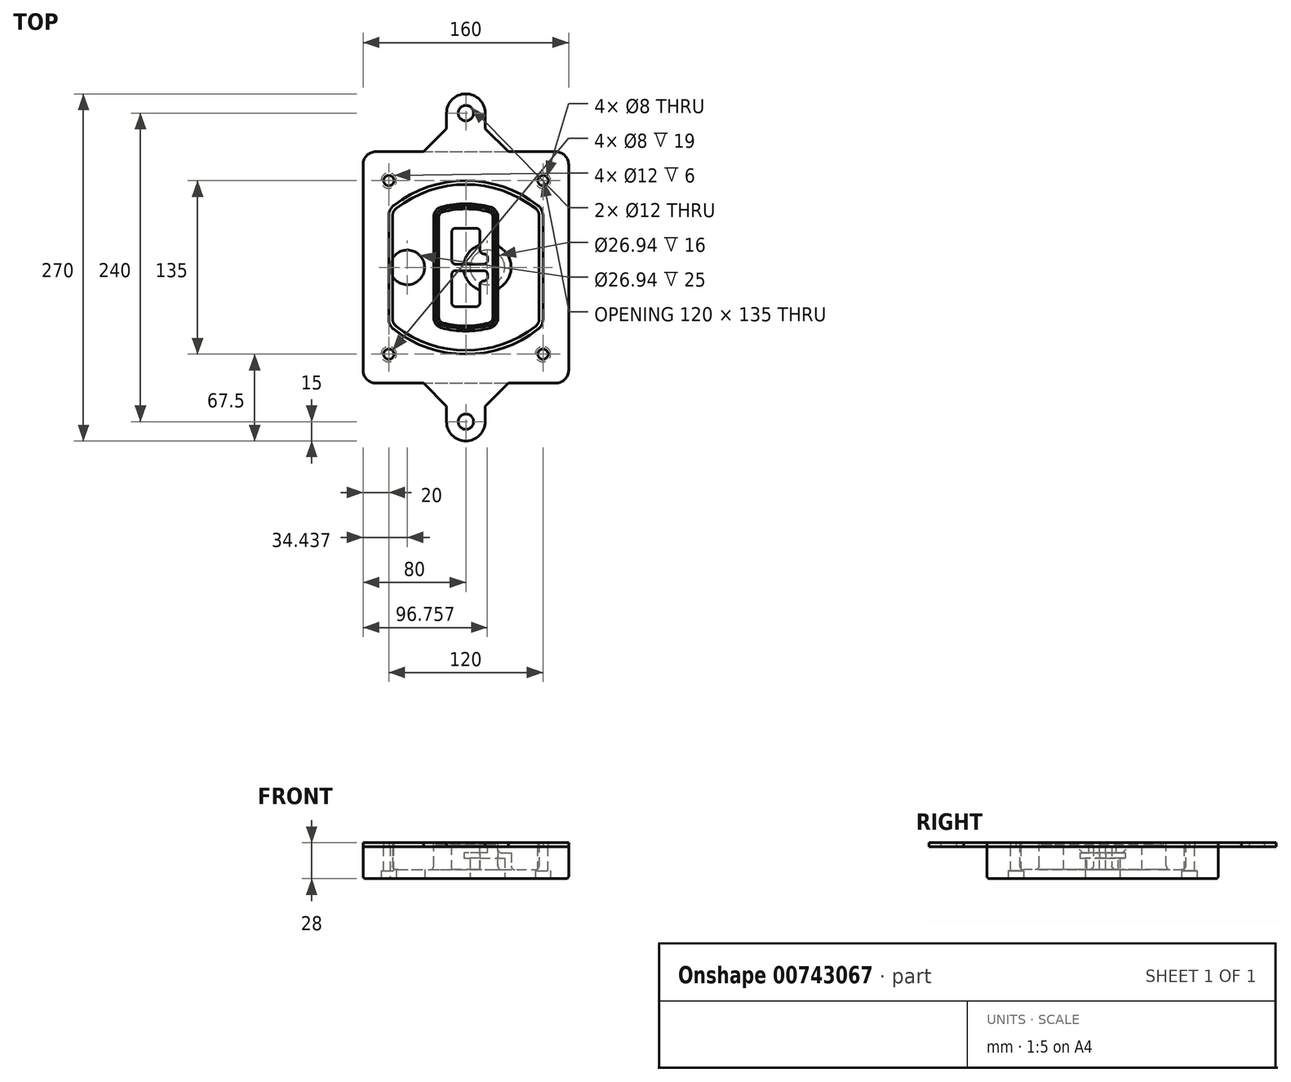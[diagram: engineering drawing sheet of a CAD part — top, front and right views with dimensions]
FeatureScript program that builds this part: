
annotation { "Feature Type Name" : "Feature", "Feature Type Description" : "" }
export const myFeature = defineFeature(function(context is Context, id is Id, definition is map)
    precondition{}
    {
        {
            var Q0;
            Q0=qCreatedBy(makeId("Top.planeOp"),FACE);
            var sketch = newSketch(context, id + "F0", { "sketchPlane" : qUnion([Q0])});
            skPoint(sketch, "E0.rect.middle", {"position": v(0, 0) * mm});
            skLineSegment(sketch, "E1.bottom", {"start": v(-70, -90) * mm, "end": v(70, -90) * mm});
            skLineSegment(sketch, "E1.top", {"start": v(-70, 90) * mm, "end": v(70, 90) * mm});
            skLineSegment(sketch, "E1.left", {"start": v(-80, -80) * mm, "end": v(-80, 80) * mm});
            skLineSegment(sketch, "E1.right", {"start": v(80, -80) * mm, "end": v(80, 80) * mm});
            skLineSegment(sketch, "E2", {"start": v(-80, 90) * mm, "end": v(80, -90) * mm, "construction": true});
            skLineSegment(sketch, "E3", {"start": v(80, 90) * mm, "end": v(-80, -90) * mm, "construction": true});
            skCircle(sketch, "E4", {"center": v(-60, 67.5) * mm, "radius": 4 * mm});
            skCircle(sketch, "E5", {"center": v(60, 67.5) * mm, "radius": 4 * mm});
            skCircle(sketch, "E6", {"center": v(60, -67.5) * mm, "radius": 4 * mm});
            skCircle(sketch, "E7", {"center": v(-60, -67.5) * mm, "radius": 4 * mm});
            skLineSegment(sketch, "E8", {"start": v(-60, 67.5) * mm, "end": v(60, 67.5) * mm, "construction": true});
            skLineSegment(sketch, "E9", {"start": v(60, 67.5) * mm, "end": v(60, -67.5) * mm, "construction": true});
            skLineSegment(sketch, "E10", {"start": v(60, -67.5) * mm, "end": v(-60, -67.5) * mm, "construction": true});
            skLineSegment(sketch, "E11", {"start": v(-60, -67.5) * mm, "end": v(-60, 67.5) * mm, "construction": true});
            skLineSegment(sketch, "E12", {"start": v(-60, 40.3) * mm, "end": v(-60, -40.3) * mm});
            skLineSegment(sketch, "E13", {"start": v(60, 40.3) * mm, "end": v(60, -40.3) * mm});
            skArc(sketch, "E14", {"start": v(56.15, 48.18) * mm, "mid": v(0, 67.5) * mm, "end": v(-56.15, 48.18) * mm});
            skArc(sketch, "E15", {"start": v(-56.15, -48.18) * mm, "mid": v(0, -67.5) * mm, "end": v(56.15, -48.18) * mm});
            skLineSegment(sketch, "E16", {"start": v(-60, 0) * mm, "end": v(60, 0) * mm, "construction": true});
            skPoint(sketch, "E17.visualSharp", {"position": v(-60, -45) * mm});
            skArc(sketch, "E17.filletArc", {"start": v(-60, -40.3) * mm, "mid": v(-58.99, -44.68) * mm, "end": v(-56.15, -48.18) * mm});
            skPoint(sketch, "E18.visualSharp", {"position": v(-60, 45) * mm});
            skArc(sketch, "E18.filletArc", {"start": v(-56.15, 48.18) * mm, "mid": v(-58.99, 44.68) * mm, "end": v(-60, 40.3) * mm});
            skPoint(sketch, "E19.visualSharp", {"position": v(60, 45) * mm});
            skArc(sketch, "E19.filletArc", {"start": v(60, 40.3) * mm, "mid": v(58.99, 44.68) * mm, "end": v(56.15, 48.18) * mm});
            skPoint(sketch, "E20.visualSharp", {"position": v(60, -45) * mm});
            skArc(sketch, "E20.filletArc", {"start": v(56.15, -48.18) * mm, "mid": v(58.99, -44.68) * mm, "end": v(60, -40.3) * mm});
            skPoint(sketch, "E21.visualSharp", {"position": v(-80, 90) * mm});
            skArc(sketch, "E21.filletArc", {"start": v(-70, 90) * mm, "mid": v(-77.07, 87.07) * mm, "end": v(-80, 80) * mm});
            skPoint(sketch, "E22.visualSharp", {"position": v(80, 90) * mm});
            skArc(sketch, "E22.filletArc", {"start": v(80, 80) * mm, "mid": v(77.07, 87.07) * mm, "end": v(70, 90) * mm});
            skPoint(sketch, "E23.visualSharp", {"position": v(80, -90) * mm});
            skArc(sketch, "E23.filletArc", {"start": v(70, -90) * mm, "mid": v(77.07, -87.07) * mm, "end": v(80, -80) * mm});
            skPoint(sketch, "E24.visualSharp", {"position": v(-80, -90) * mm});
            skArc(sketch, "E24.filletArc", {"start": v(-80, -80) * mm, "mid": v(-77.07, -87.07) * mm, "end": v(-70, -90) * mm});
            skArc(sketch, "E25.0", {"start": v(57, 40.3) * mm, "mid": v(56.3, 43.36) * mm, "end": v(54.3, 45.81) * mm});
            skLineSegment(sketch, "E25.1", {"start": v(57, 40.3) * mm, "end": v(57, -40.3) * mm});
            skArc(sketch, "E25.2", {"start": v(54.3, -45.81) * mm, "mid": v(56.3, -43.36) * mm, "end": v(57, -40.3) * mm});
            skArc(sketch, "E25.3", {"start": v(-54.3, -45.81) * mm, "mid": v(0, -64.5) * mm, "end": v(54.3, -45.81) * mm});
            skArc(sketch, "E25.4", {"start": v(-57, -40.3) * mm, "mid": v(-56.3, -43.36) * mm, "end": v(-54.3, -45.81) * mm});
            skArc(sketch, "E25.5", {"start": v(54.3, 45.81) * mm, "mid": v(0, 64.5) * mm, "end": v(-54.3, 45.81) * mm});
            skLineSegment(sketch, "E25.6", {"start": v(-57, 40.3) * mm, "end": v(-57, -40.3) * mm});
            skArc(sketch, "E25.7", {"start": v(-54.3, 45.81) * mm, "mid": v(-56.3, 43.36) * mm, "end": v(-57, 40.3) * mm});
            skArc(sketch, "E26.0", {"start": v(-58.62, 51.33) * mm, "mid": v(-62.58, 46.43) * mm, "end": v(-64, 40.3) * mm});
            skArc(sketch, "E26.1", {"start": v(58.62, 51.33) * mm, "mid": v(0, 71.5) * mm, "end": v(-58.62, 51.33) * mm});
            skArc(sketch, "E26.2", {"start": v(64, 40.3) * mm, "mid": v(62.58, 46.43) * mm, "end": v(58.62, 51.33) * mm});
            skLineSegment(sketch, "E26.3", {"start": v(64, 40.3) * mm, "end": v(64, -40.3) * mm});
            skArc(sketch, "E26.4", {"start": v(58.62, -51.33) * mm, "mid": v(62.58, -46.43) * mm, "end": v(64, -40.3) * mm});
            skLineSegment(sketch, "E26.5", {"start": v(-64, 40.3) * mm, "end": v(-64, -40.3) * mm});
            skArc(sketch, "E26.6", {"start": v(-58.62, -51.33) * mm, "mid": v(0, -71.5) * mm, "end": v(58.62, -51.33) * mm});
            skArc(sketch, "E26.7", {"start": v(-64, -40.3) * mm, "mid": v(-62.58, -46.43) * mm, "end": v(-58.62, -51.33) * mm});
            skSolve(sketch);
        }
        {
            var Q0;
            Q0=makeQuery(id+"F0.imprint","IMPRINT",FACE,{"disambiguationData":[TD([[makeQuery(id+"F0.imprint","IMPRINT",EDGE,{"derivedFrom":sQuery(id+"F0.wireOp",EDGE,"E1.bottom")}),1.0]])]});
            var Q1;
            Q1=makeQuery(id+"F0.imprint","IMPRINT",FACE,{"disambiguationData":[TD([[makeQuery(id+"F0.imprint","IMPRINT",EDGE,{"derivedFrom":sQuery(id+"F0.wireOp",EDGE,"E12")}),1.0]])]});
            var Q2;
            Q2=makeQuery(id+"F0.imprint","IMPRINT",FACE,{"disambiguationData":[TD([[makeQuery(id+"F0.imprint","IMPRINT",EDGE,{"derivedFrom":sQuery(id+"F0.wireOp",EDGE,"E25.0")}),1.0]])]});
            var Q3;
            Q3=makeQuery(id+"F0.imprint","IMPRINT",FACE,{"disambiguationData":[TD([[makeQuery(id+"F0.imprint","IMPRINT",EDGE,{"derivedFrom":sQuery(id+"F0.wireOp",EDGE,"E12")}),-1.0]])]});
            extrude(context, id + "F1", {"entities" : qUnion([Q0, Q1, Q2, Q3]), "oppositeDirection" : true, "depth" : 25 * mm});
        }
        {
            var Q0;
            Q0=makeQuery(id+"F0.imprint","IMPRINT",FACE,{"disambiguationData":[TD([[makeQuery(id+"F0.imprint","IMPRINT",EDGE,{"derivedFrom":sQuery(id+"F0.wireOp",EDGE,"E12")}),1.0]])]});
            extrude(context, id + "F2", {"entities" : qUnion([Q0]), "operationType" : NewBodyOperationType.ADD, "depth" : 3 * mm});
        }
        {
            var Q0;
            Q0=makeQuery(id+"F0.imprint","IMPRINT",FACE,{"disambiguationData":[TD([[makeQuery(id+"F0.imprint","IMPRINT",EDGE,{"derivedFrom":sQuery(id+"F0.wireOp",EDGE,"E25.0")}),1.0]])]});
            extrude(context, id + "F3", {"entities" : qUnion([Q0]), "operationType" : NewBodyOperationType.REMOVE, "oppositeDirection" : true, "depth" : 18 * mm});
        }
        {
            var Q0;
            Q0=makeQuery(id+"F2.opExtrude","CAP_FACE",FACE,{"disambiguationData":[OSD([sQuery(id+"F0.wireOp",EDGE,"E12"),sQuery(id+"F0.wireOp",EDGE,"E13"),sQuery(id+"F0.wireOp",EDGE,"E14"),sQuery(id+"F0.wireOp",EDGE,"E15"),sQuery(id+"F0.wireOp",EDGE,"E17.filletArc"),sQuery(id+"F0.wireOp",EDGE,"E18.filletArc"),sQuery(id+"F0.wireOp",EDGE,"E19.filletArc"),sQuery(id+"F0.wireOp",EDGE,"E20.filletArc"),sQuery(id+"F0.wireOp",EDGE,"E25.0"),sQuery(id+"F0.wireOp",EDGE,"E25.1"),sQuery(id+"F0.wireOp",EDGE,"E25.2"),sQuery(id+"F0.wireOp",EDGE,"E25.3"),sQuery(id+"F0.wireOp",EDGE,"E25.4"),sQuery(id+"F0.wireOp",EDGE,"E25.5"),sQuery(id+"F0.wireOp",EDGE,"E25.6"),sQuery(id+"F0.wireOp",EDGE,"E25.7")])],"isStart":false});
            var sketch = newSketch(context, id + "F4", { "sketchPlane" : qUnion([Q0])});
            skArc(sketch, "E27.0", {"start": v(-19.08, -46.97) * mm, "mid": v(0, -49.5) * mm, "end": v(19.08, -46.97) * mm});
            skArc(sketch, "E28.0", {"start": v(19.08, 46.97) * mm, "mid": v(0, 49.5) * mm, "end": v(-19.08, 46.97) * mm});
            skLineSegment(sketch, "E29", {"start": v(-25, 39.25) * mm, "end": v(-25, -39.25) * mm});
            skLineSegment(sketch, "E30", {"start": v(25, 39.25) * mm, "end": v(25, -39.25) * mm});
            skLineSegment(sketch, "E31", {"start": v(-25, 45.1) * mm, "end": v(25, 45.1) * mm, "construction": true});
            skLineSegment(sketch, "E32", {"start": v(-25, -45.1) * mm, "end": v(25, -45.1) * mm, "construction": true});
            skPoint(sketch, "E33.visualSharp", {"position": v(-25, 45.1) * mm});
            skArc(sketch, "E33.filletArc", {"start": v(-19.08, 46.97) * mm, "mid": v(-23.35, 44.11) * mm, "end": v(-25, 39.25) * mm});
            skPoint(sketch, "E34.visualSharp", {"position": v(25, 45.1) * mm});
            skArc(sketch, "E34.filletArc", {"start": v(25, 39.25) * mm, "mid": v(23.35, 44.11) * mm, "end": v(19.08, 46.97) * mm});
            skPoint(sketch, "E35.visualSharp", {"position": v(25, -45.1) * mm});
            skArc(sketch, "E35.filletArc", {"start": v(19.08, -46.97) * mm, "mid": v(23.35, -44.11) * mm, "end": v(25, -39.25) * mm});
            skPoint(sketch, "E36.visualSharp", {"position": v(-25, -45.1) * mm});
            skArc(sketch, "E36.filletArc", {"start": v(-25, -39.25) * mm, "mid": v(-23.35, -44.11) * mm, "end": v(-19.08, -46.97) * mm});
            skArc(sketch, "E37.0", {"start": v(54.3, 45.81) * mm, "mid": v(0, 64.5) * mm, "end": v(-54.3, 45.81) * mm});
            skArc(sketch, "E37.1", {"start": v(-54.3, 45.81) * mm, "mid": v(-56.3, 43.36) * mm, "end": v(-57, 40.3) * mm});
            skLineSegment(sketch, "E37.2", {"start": v(-57, 40.3) * mm, "end": v(-57, -40.3) * mm});
            skArc(sketch, "E37.3", {"start": v(-57, -40.3) * mm, "mid": v(-56.3, -43.36) * mm, "end": v(-54.3, -45.81) * mm});
            skArc(sketch, "E37.4", {"start": v(-54.3, -45.81) * mm, "mid": v(0, -64.5) * mm, "end": v(54.3, -45.81) * mm});
            skArc(sketch, "E37.5", {"start": v(54.3, -45.81) * mm, "mid": v(56.3, -43.36) * mm, "end": v(57, -40.3) * mm});
            skLineSegment(sketch, "E37.6", {"start": v(57, 40.3) * mm, "end": v(57, -40.3) * mm});
            skArc(sketch, "E37.7", {"start": v(57, 40.3) * mm, "mid": v(56.3, 43.36) * mm, "end": v(54.3, 45.81) * mm});
            skLineSegment(sketch, "E38.0", {"start": v(23, 39.25) * mm, "end": v(23, -39.25) * mm});
            skArc(sketch, "E38.1", {"start": v(18.56, -45.04) * mm, "mid": v(21.76, -42.9) * mm, "end": v(23, -39.25) * mm});
            skArc(sketch, "E38.2", {"start": v(-18.56, -45.04) * mm, "mid": v(0, -47.5) * mm, "end": v(18.56, -45.04) * mm});
            skArc(sketch, "E38.3", {"start": v(-23, -39.25) * mm, "mid": v(-21.76, -42.9) * mm, "end": v(-18.56, -45.04) * mm});
            skLineSegment(sketch, "E38.4", {"start": v(-23, 39.25) * mm, "end": v(-23, -39.25) * mm});
            skArc(sketch, "E38.5", {"start": v(23, 39.25) * mm, "mid": v(21.76, 42.9) * mm, "end": v(18.56, 45.04) * mm});
            skArc(sketch, "E38.6", {"start": v(-18.56, 45.04) * mm, "mid": v(-21.76, 42.9) * mm, "end": v(-23, 39.25) * mm});
            skArc(sketch, "E38.7", {"start": v(18.56, 45.04) * mm, "mid": v(0, 47.5) * mm, "end": v(-18.56, 45.04) * mm});
            skArc(sketch, "E39.0", {"start": v(21, 39.25) * mm, "mid": v(20.18, 41.68) * mm, "end": v(18.04, 43.1) * mm});
            skLineSegment(sketch, "E39.1", {"start": v(21, 39.25) * mm, "end": v(21, -39.25) * mm});
            skArc(sketch, "E39.2", {"start": v(18.04, -43.1) * mm, "mid": v(20.18, -41.68) * mm, "end": v(21, -39.25) * mm});
            skArc(sketch, "E39.3", {"start": v(-18.04, -43.1) * mm, "mid": v(0, -45.5) * mm, "end": v(18.04, -43.1) * mm});
            skArc(sketch, "E39.4", {"start": v(-21, -39.25) * mm, "mid": v(-20.18, -41.68) * mm, "end": v(-18.04, -43.1) * mm});
            skArc(sketch, "E39.5", {"start": v(18.04, 43.1) * mm, "mid": v(0, 45.5) * mm, "end": v(-18.04, 43.1) * mm});
            skLineSegment(sketch, "E39.6", {"start": v(-21, 39.25) * mm, "end": v(-21, -39.25) * mm});
            skArc(sketch, "E39.7", {"start": v(-18.04, 43.1) * mm, "mid": v(-20.18, 41.68) * mm, "end": v(-21, 39.25) * mm});
            skLineSegment(sketch, "E40", {"start": v(-25, 0) * mm, "end": v(25, 0) * mm, "construction": true});
            skLineSegment(sketch, "E41", {"start": v(-11, 5.5) * mm, "end": v(-11, 27.5) * mm});
            skLineSegment(sketch, "E42", {"start": v(-8, 30.5) * mm, "end": v(8, 30.5) * mm});
            skLineSegment(sketch, "E43", {"start": v(11, 27.5) * mm, "end": v(11, 13.5) * mm});
            skLineSegment(sketch, "E44", {"start": v(14, 10.5) * mm, "end": v(14, 10.5) * mm});
            skLineSegment(sketch, "E45", {"start": v(17, 7.5) * mm, "end": v(17, 5.5) * mm});
            skLineSegment(sketch, "E46", {"start": v(14, 2.5) * mm, "end": v(-8, 2.5) * mm});
            skPoint(sketch, "E47.visualSharp", {"position": v(-11, 30.5) * mm});
            skArc(sketch, "E47.filletArc", {"start": v(-8, 30.5) * mm, "mid": v(-10.12, 29.62) * mm, "end": v(-11, 27.5) * mm});
            skPoint(sketch, "E48.visualSharp", {"position": v(11, 30.5) * mm});
            skArc(sketch, "E48.filletArc", {"start": v(11, 27.5) * mm, "mid": v(10.12, 29.62) * mm, "end": v(8, 30.5) * mm});
            skPoint(sketch, "E49.visualSharp", {"position": v(11, 10.5) * mm});
            skArc(sketch, "E49.filletArc", {"start": v(11, 13.5) * mm, "mid": v(11.88, 11.38) * mm, "end": v(14, 10.5) * mm});
            skPoint(sketch, "E50.visualSharp", {"position": v(17, 10.5) * mm});
            skArc(sketch, "E50.filletArc", {"start": v(17, 7.5) * mm, "mid": v(16.12, 9.62) * mm, "end": v(14, 10.5) * mm});
            skPoint(sketch, "E51.visualSharp", {"position": v(17, 2.5) * mm});
            skArc(sketch, "E51.filletArc", {"start": v(14, 2.5) * mm, "mid": v(16.12, 3.38) * mm, "end": v(17, 5.5) * mm});
            skPoint(sketch, "E52.visualSharp", {"position": v(-11, 2.5) * mm});
            skArc(sketch, "E52.filletArc", {"start": v(-11, 5.5) * mm, "mid": v(-10.12, 3.38) * mm, "end": v(-8, 2.5) * mm});
            skLineSegment(sketch, "E53.0.MirrorCS", {"start": v(14, -2.5) * mm, "end": v(-8, -2.5) * mm});
            skArc(sketch, "E54.0.MirrorCS", {"start": v(-11, -5.5) * mm, "mid": v(-10.12, -3.38) * mm, "end": v(-8, -2.5) * mm});
            skLineSegment(sketch, "E55.0.MirrorCS", {"start": v(-11, -5.5) * mm, "end": v(-11, -27.5) * mm});
            skArc(sketch, "E56.0.MirrorCS", {"start": v(-8, -30.5) * mm, "mid": v(-10.12, -29.62) * mm, "end": v(-11, -27.5) * mm});
            skLineSegment(sketch, "E57.0.MirrorCS", {"start": v(-8, -30.5) * mm, "end": v(8, -30.5) * mm});
            skArc(sketch, "E58.0.MirrorCS", {"start": v(11, -27.5) * mm, "mid": v(10.12, -29.62) * mm, "end": v(8, -30.5) * mm});
            skLineSegment(sketch, "E59.0.MirrorCS", {"start": v(11, -27.5) * mm, "end": v(11, -13.5) * mm});
            skArc(sketch, "E60.0.MirrorCS", {"start": v(11, -13.5) * mm, "mid": v(11.88, -11.38) * mm, "end": v(14, -10.5) * mm});
            skArc(sketch, "E61.0.MirrorCS", {"start": v(17, -7.5) * mm, "mid": v(16.12, -9.62) * mm, "end": v(14, -10.5) * mm});
            skLineSegment(sketch, "E62.0.MirrorCS", {"start": v(17, -7.5) * mm, "end": v(17, -5.5) * mm});
            skArc(sketch, "E63.0.MirrorCS", {"start": v(14, -2.5) * mm, "mid": v(16.12, -3.38) * mm, "end": v(17, -5.5) * mm});
            skSolve(sketch);
        }
        {
            var Q0;
            Q0=makeQuery(id+"F4.imprint","IMPRINT",FACE,{"disambiguationData":[TD([[makeQuery(id+"F4.imprint","IMPRINT",EDGE,{"derivedFrom":sQuery(id+"F4.wireOp",EDGE,"E27.0")}),1.0]])]});
            var Q1;
            Q1=makeQuery(id+"F4.imprint","IMPRINT",FACE,{"disambiguationData":[TD([[makeQuery(id+"F4.imprint","IMPRINT",EDGE,{"derivedFrom":sQuery(id+"F4.wireOp",EDGE,"E38.0")}),-1.0]])]});
            var Q2;
            Q2=makeQuery(id+"F4.imprint","IMPRINT",FACE,{"disambiguationData":[TD([[makeQuery(id+"F4.imprint","IMPRINT",EDGE,{"derivedFrom":sQuery(id+"F4.wireOp",EDGE,"E39.0")}),1.0]])]});
            extrude(context, id + "F5", {"entities" : qUnion([Q0, Q1, Q2]), "operationType" : NewBodyOperationType.ADD, "endBound" : BoundingType.UP_TO_NEXT, "oppositeDirection" : true, "depth" : 25 * mm});
        }
        {
            var Q0;
            Q0=makeQuery(id+"F4.imprint","IMPRINT",FACE,{"disambiguationData":[TD([[makeQuery(id+"F4.imprint","IMPRINT",EDGE,{"derivedFrom":sQuery(id+"F4.wireOp",EDGE,"E38.0")}),-1.0]])]});
            extrude(context, id + "F6", {"entities" : qUnion([Q0]), "operationType" : NewBodyOperationType.REMOVE, "oppositeDirection" : true, "depth" : 2 * mm});
        }
        {
            var Q0;
            Q0=makeQuery(id+"F1.opExtrude","CAP_FACE",FACE,{"disambiguationData":[OSD([sQuery(id+"F0.wireOp",EDGE,"E1.bottom"),sQuery(id+"F0.wireOp",EDGE,"E1.top"),sQuery(id+"F0.wireOp",EDGE,"E1.left"),sQuery(id+"F0.wireOp",EDGE,"E1.right"),sQuery(id+"F0.wireOp",EDGE,"E4"),sQuery(id+"F0.wireOp",EDGE,"E5"),sQuery(id+"F0.wireOp",EDGE,"E6"),sQuery(id+"F0.wireOp",EDGE,"E7"),sQuery(id+"F0.wireOp",EDGE,"E21.filletArc"),sQuery(id+"F0.wireOp",EDGE,"E22.filletArc"),sQuery(id+"F0.wireOp",EDGE,"E23.filletArc"),sQuery(id+"F0.wireOp",EDGE,"E24.filletArc")])],"isStart":false});
            var sketch = newSketch(context, id + "F7", { "sketchPlane" : qUnion([Q0])});
            skCircle(sketch, "E64", {"center": v(16.76, 0) * mm, "radius": 13.47 * mm});
            skCircle(sketch, "E65", {"center": v(-45.56, 0) * mm, "radius": 13.47 * mm});
            skLineSegment(sketch, "E66", {"start": v(80, 0) * mm, "end": v(-80, 0) * mm});
            skCircle(sketch, "E67", {"center": v(16.76, 0) * mm, "radius": 18.47 * mm});
            skCircle(sketch, "E68", {"center": v(60, -67.5) * mm, "radius": 6 * mm});
            skCircle(sketch, "E69", {"center": v(-60, -67.5) * mm, "radius": 6 * mm});
            skCircle(sketch, "E70", {"center": v(-60, 67.5) * mm, "radius": 6 * mm});
            skCircle(sketch, "E71", {"center": v(60, 67.5) * mm, "radius": 6 * mm});
            skSolve(sketch);
        }
        {
            var Q0;
            {var subQ1=sQuery(id+"F7.wireOp",EDGE,"E66");var subQ4=sQuery(id+"F7.wireOp",EDGE,"E64");var subQ6=makeQuery(id+"F7.imprint","INTERSECT",VERTEX,{"disambiguationData":[OD(0.0)],"derivedFrom":[subQ4,subQ1]});Q0=makeQuery(id+"F7.imprint","IMPRINT",FACE,{"disambiguationData":[TD([[makeQuery(id+"F7.imprint","IMPRINT",EDGE,{"disambiguationData":[TD([[subQ6,-1.0]])],"derivedFrom":subQ4}),-1.0]])]});}
            var Q1;
            {var subQ0=sQuery(id+"F7.wireOp",EDGE,"E66");var subQ1=sQuery(id+"F7.wireOp",EDGE,"E64");var subQ3=makeQuery(id+"F7.imprint","INTERSECT",VERTEX,{"disambiguationData":[OD(0.0)],"derivedFrom":[subQ1,subQ0]});Q1=makeQuery(id+"F7.imprint","IMPRINT",FACE,{"disambiguationData":[TD([[makeQuery(id+"F7.imprint","IMPRINT",EDGE,{"disambiguationData":[TD([[subQ3,-1.0]])],"derivedFrom":subQ1}),1.0]])]});}
            var Q2;
            {var subQ0=sQuery(id+"F7.wireOp",EDGE,"E66");var subQ1=sQuery(id+"F7.wireOp",EDGE,"E64");var subQ3=makeQuery(id+"F7.imprint","INTERSECT",VERTEX,{"disambiguationData":[OD(0.0)],"derivedFrom":[subQ1,subQ0]});Q2=makeQuery(id+"F7.imprint","IMPRINT",FACE,{"disambiguationData":[TD([[makeQuery(id+"F7.imprint","IMPRINT",EDGE,{"disambiguationData":[TD([[subQ3,1.0]])],"derivedFrom":subQ1}),1.0]])]});}
            var Q3;
            {var subQ1=sQuery(id+"F7.wireOp",EDGE,"E66");var subQ4=sQuery(id+"F7.wireOp",EDGE,"E64");var subQ6=makeQuery(id+"F7.imprint","INTERSECT",VERTEX,{"disambiguationData":[OD(0.0)],"derivedFrom":[subQ4,subQ1]});Q3=makeQuery(id+"F7.imprint","IMPRINT",FACE,{"disambiguationData":[TD([[makeQuery(id+"F7.imprint","IMPRINT",EDGE,{"disambiguationData":[TD([[subQ6,1.0]])],"derivedFrom":subQ4}),-1.0]])]});}
            extrude(context, id + "F8", {"entities" : qUnion([Q0, Q1, Q2, Q3]), "operationType" : NewBodyOperationType.ADD, "oppositeDirection" : true, "depth" : 20 * mm});
        }
        {
            var Q0;
            {var subQ0=sQuery(id+"F7.wireOp",EDGE,"E66");var subQ1=sQuery(id+"F7.wireOp",EDGE,"E64");var subQ3=makeQuery(id+"F7.imprint","INTERSECT",VERTEX,{"disambiguationData":[OD(0.0)],"derivedFrom":[subQ1,subQ0]});Q0=makeQuery(id+"F7.imprint","IMPRINT",FACE,{"disambiguationData":[TD([[makeQuery(id+"F7.imprint","IMPRINT",EDGE,{"disambiguationData":[TD([[subQ3,-1.0]])],"derivedFrom":subQ1}),1.0]])]});}
            var Q1;
            {var subQ0=sQuery(id+"F7.wireOp",EDGE,"E66");var subQ1=sQuery(id+"F7.wireOp",EDGE,"E64");var subQ3=makeQuery(id+"F7.imprint","INTERSECT",VERTEX,{"disambiguationData":[OD(0.0)],"derivedFrom":[subQ1,subQ0]});Q1=makeQuery(id+"F7.imprint","IMPRINT",FACE,{"disambiguationData":[TD([[makeQuery(id+"F7.imprint","IMPRINT",EDGE,{"disambiguationData":[TD([[subQ3,1.0]])],"derivedFrom":subQ1}),1.0]])]});}
            extrude(context, id + "F9", {"entities" : qUnion([Q0, Q1]), "operationType" : NewBodyOperationType.REMOVE, "oppositeDirection" : true, "depth" : 16 * mm});
        }
        {
            var Q0;
            {var subQ0=sQuery(id+"F7.wireOp",EDGE,"E66");var subQ1=sQuery(id+"F7.wireOp",EDGE,"E65");var subQ3=makeQuery(id+"F7.imprint","INTERSECT",VERTEX,{"disambiguationData":[OD(0.0)],"derivedFrom":[subQ1,subQ0]});Q0=makeQuery(id+"F7.imprint","IMPRINT",FACE,{"disambiguationData":[TD([[makeQuery(id+"F7.imprint","IMPRINT",EDGE,{"disambiguationData":[TD([[subQ3,-1.0]])],"derivedFrom":subQ1}),1.0]])]});}
            var Q1;
            {var subQ0=sQuery(id+"F7.wireOp",EDGE,"E66");var subQ1=sQuery(id+"F7.wireOp",EDGE,"E65");var subQ3=makeQuery(id+"F7.imprint","INTERSECT",VERTEX,{"disambiguationData":[OD(0.0)],"derivedFrom":[subQ1,subQ0]});Q1=makeQuery(id+"F7.imprint","IMPRINT",FACE,{"disambiguationData":[TD([[makeQuery(id+"F7.imprint","IMPRINT",EDGE,{"disambiguationData":[TD([[subQ3,1.0]])],"derivedFrom":subQ1}),1.0]])]});}
            extrude(context, id + "F10", {"entities" : qUnion([Q0, Q1]), "operationType" : NewBodyOperationType.REMOVE, "oppositeDirection" : true, "depth" : 25 * mm});
        }
        {
            var Q0;
            Q0=makeQuery(id+"F7.imprint","IMPRINT",FACE,{"disambiguationData":[TD([[makeQuery(id+"F7.imprint","IMPRINT",EDGE,{"derivedFrom":sQuery(id+"F7.wireOp",EDGE,"E68")}),1.0]])]});
            var Q1;
            Q1=makeQuery(id+"F7.imprint","IMPRINT",FACE,{"disambiguationData":[TD([[makeQuery(id+"F7.imprint","IMPRINT",EDGE,{"derivedFrom":makeQuery(id+"F1.opExtrude","CAP_EDGE",EDGE,{"disambiguationData":[OSD([sQuery(id+"F0.wireOp",EDGE,"E5")])],"isStart":false})}),-1.0]])]});
            var Q2;
            Q2=makeQuery(id+"F7.imprint","IMPRINT",FACE,{"disambiguationData":[TD([[makeQuery(id+"F7.imprint","IMPRINT",EDGE,{"derivedFrom":sQuery(id+"F7.wireOp",EDGE,"E69")}),1.0]])]});
            var Q3;
            Q3=makeQuery(id+"F7.imprint","IMPRINT",FACE,{"disambiguationData":[TD([[makeQuery(id+"F7.imprint","IMPRINT",EDGE,{"derivedFrom":makeQuery(id+"F1.opExtrude","CAP_EDGE",EDGE,{"disambiguationData":[OSD([sQuery(id+"F0.wireOp",EDGE,"E4")])],"isStart":false})}),-1.0]])]});
            var Q4;
            Q4=makeQuery(id+"F7.imprint","IMPRINT",FACE,{"disambiguationData":[TD([[makeQuery(id+"F7.imprint","IMPRINT",EDGE,{"derivedFrom":sQuery(id+"F7.wireOp",EDGE,"E70")}),1.0]])]});
            var Q5;
            Q5=makeQuery(id+"F7.imprint","IMPRINT",FACE,{"disambiguationData":[TD([[makeQuery(id+"F7.imprint","IMPRINT",EDGE,{"derivedFrom":makeQuery(id+"F1.opExtrude","CAP_EDGE",EDGE,{"disambiguationData":[OSD([sQuery(id+"F0.wireOp",EDGE,"E7")])],"isStart":false})}),-1.0]])]});
            var Q6;
            Q6=makeQuery(id+"F7.imprint","IMPRINT",FACE,{"disambiguationData":[TD([[makeQuery(id+"F7.imprint","IMPRINT",EDGE,{"derivedFrom":sQuery(id+"F7.wireOp",EDGE,"E71")}),1.0]])]});
            var Q7;
            Q7=makeQuery(id+"F7.imprint","IMPRINT",FACE,{"disambiguationData":[TD([[makeQuery(id+"F7.imprint","IMPRINT",EDGE,{"derivedFrom":makeQuery(id+"F1.opExtrude","CAP_EDGE",EDGE,{"disambiguationData":[OSD([sQuery(id+"F0.wireOp",EDGE,"E6")])],"isStart":false})}),-1.0]])]});
            extrude(context, id + "F11", {"entities" : qUnion([Q0, Q1, Q2, Q3, Q4, Q5, Q6, Q7]), "operationType" : NewBodyOperationType.REMOVE, "oppositeDirection" : true, "depth" : 6 * mm});
        }
        {
            var Q0;
            Q0=makeQuery(id+"F9.boolean.opBoolean","COPY",FACE,{"derivedFrom":makeQuery(id+"F9.opExtrude","CAP_FACE",FACE,{"disambiguationData":[OSD([sQuery(id+"F7.wireOp",EDGE,"E64")])],"isStart":false})});
            var sketch = newSketch(context, id + "F12", { "sketchPlane" : qUnion([Q0])});
            skArc(sketch, "E72.0", {"start": v(11, 17.55) * mm, "mid": v(2.57, 11.82) * mm, "end": v(-1.54, 2.5) * mm});
            skArc(sketch, "E72.1", {"start": v(-1.54, -2.5) * mm, "mid": v(2.57, -11.82) * mm, "end": v(11, -17.55) * mm});
            skLineSegment(sketch, "E73", {"start": v(-1.54, -2.5) * mm, "end": v(14, -2.5) * mm});
            skLineSegment(sketch, "E74.0", {"start": v(14, 2.5) * mm, "end": v(-1.54, 2.5) * mm});
            skArc(sketch, "E74.1", {"start": v(14, 2.5) * mm, "mid": v(16.12, 3.38) * mm, "end": v(17, 5.5) * mm});
            skLineSegment(sketch, "E74.2", {"start": v(17, 7.5) * mm, "end": v(17, 5.5) * mm});
            skArc(sketch, "E74.3", {"start": v(17, 7.5) * mm, "mid": v(16.12, 9.62) * mm, "end": v(14, 10.5) * mm});
            skArc(sketch, "E74.4", {"start": v(11, 13.5) * mm, "mid": v(11.88, 11.38) * mm, "end": v(14, 10.5) * mm});
            skLineSegment(sketch, "E74.5", {"start": v(11, 17.55) * mm, "end": v(11, 13.5) * mm});
            skLineSegment(sketch, "E74.7", {"start": v(14, -2.5) * mm, "end": v(-1.54, -2.5) * mm});
            skArc(sketch, "E74.8", {"start": v(14, -2.5) * mm, "mid": v(16.12, -3.38) * mm, "end": v(17, -5.5) * mm});
            skLineSegment(sketch, "E74.9", {"start": v(17, -7.5) * mm, "end": v(17, -5.5) * mm});
            skArc(sketch, "E74.10", {"start": v(17, -7.5) * mm, "mid": v(16.12, -9.62) * mm, "end": v(14, -10.5) * mm});
            skArc(sketch, "E74.11", {"start": v(11, -13.5) * mm, "mid": v(11.88, -11.38) * mm, "end": v(14, -10.5) * mm});
            skLineSegment(sketch, "E74.12", {"start": v(11, -17.55) * mm, "end": v(11, -13.5) * mm});
            skPoint(sketch, "E75.orphan", {"position": v(11, -27.5) * mm});
            skPoint(sketch, "E76.orphan", {"position": v(-8, -2.5) * mm});
            skPoint(sketch, "E77.orphan", {"position": v(-8, 2.5) * mm});
            skPoint(sketch, "E78.orphan", {"position": v(11, 27.5) * mm});
            skSolve(sketch);
        }
        {
            var Q0;
            {var subQ7=sQuery(id+"F12.wireOp",EDGE,"E72.0");var subQ14=sQuery(id+"F12.wireOp",EDGE,"E72.1");var subQ16=sQuery(id+"F12.wireOp",EDGE,"E74.1");var subQ18=sQuery(id+"F12.wireOp",EDGE,"E74.8");Q0=qUnion([makeQuery(id+"F12.imprint","IMPRINT",FACE,{"disambiguationData":[TD([[makeQuery(id+"F12.imprint","IMPRINT",EDGE,{"derivedFrom":subQ7}),1.0]])]}),makeQuery(id+"F12.imprint","IMPRINT",FACE,{"disambiguationData":[TD([[makeQuery(id+"F12.imprint","IMPRINT",EDGE,{"derivedFrom":subQ14}),1.0]])]}),makeQuery(id+"F12.imprint","IMPRINT",FACE,{"disambiguationData":[TD([[makeQuery(id+"F12.imprint","IMPRINT",EDGE,{"derivedFrom":subQ16}),1.0]])]}),makeQuery(id+"F12.imprint","IMPRINT",FACE,{"disambiguationData":[TD([[makeQuery(id+"F12.imprint","IMPRINT",EDGE,{"derivedFrom":subQ18}),-1.0]])]})]);}
            var Q1;
            Q1=makeQuery(id+"F5.boolean.opBoolean","SPLIT",FACE,{"disambiguationData":[TD([makeQuery(id+"F5.opExtrude","SWEPT_FACE",FACE,{"disambiguationData":[OSD([sQuery(id+"F4.wireOp",EDGE,"E41")])]})])],"derivedFrom":makeQuery(id+"F3.boolean.opBoolean","COPY",FACE,{"derivedFrom":makeQuery(id+"F3.opExtrude","CAP_FACE",FACE,{"disambiguationData":[OSD([sQuery(id+"F0.wireOp",EDGE,"E25.0"),sQuery(id+"F0.wireOp",EDGE,"E25.1"),sQuery(id+"F0.wireOp",EDGE,"E25.2"),sQuery(id+"F0.wireOp",EDGE,"E25.3"),sQuery(id+"F0.wireOp",EDGE,"E25.4"),sQuery(id+"F0.wireOp",EDGE,"E25.5"),sQuery(id+"F0.wireOp",EDGE,"E25.6"),sQuery(id+"F0.wireOp",EDGE,"E25.7")])],"isStart":false})})});
            extrude(context, id + "F13", {"entities" : qUnion([Q0]), "operationType" : NewBodyOperationType.REMOVE, "endBound" : BoundingType.UP_TO_SURFACE, "endBoundEntityFace" : qUnion([Q1]), "depth" : 25 * mm});
        }
        {
            var Q0;
            Q0=makeQuery(id+"F3.boolean.opBoolean","COPY",EDGE,{"derivedFrom":makeQuery(id+"F3.opExtrude","CAP_EDGE",EDGE,{"disambiguationData":[OSD([sQuery(id+"F0.wireOp",EDGE,"E25.6")])],"isStart":false})});
            var Q1;
            Q1=makeQuery(id+"F8.boolean.opBoolean","INTERSECT",EDGE,{"derivedFrom":[makeQuery(id+"F5.opExtrude","SWEPT_FACE",FACE,{"disambiguationData":[OSD([sQuery(id+"F4.wireOp",EDGE,"E30")])]}),makeQuery(id+"F8.opExtrude","CAP_FACE",FACE,{"disambiguationData":[OSD([sQuery(id+"F7.wireOp",EDGE,"E67")])],"isStart":false})]});
            var Q2;
            Q2=makeQuery(id+"F8.boolean.opBoolean","INTERSECT",EDGE,{"disambiguationData":[OD(1.0)],"derivedFrom":[makeQuery(id+"F5.opExtrude","SWEPT_FACE",FACE,{"disambiguationData":[OSD([sQuery(id+"F4.wireOp",EDGE,"E30")])]}),makeQuery(id+"F8.opExtrude","SWEPT_FACE",FACE,{"disambiguationData":[OSD([sQuery(id+"F7.wireOp",EDGE,"E67")])]})]});
            var Q3;
            {var subQ0=sQuery(id+"F4.wireOp",EDGE,"E30");Q3=makeQuery(id+"F8.boolean.opBoolean","SPLIT",EDGE,{"disambiguationData":[TD([makeQuery(id+"F5.opExtrude","SWEPT_FACE",FACE,{"disambiguationData":[OSD([sQuery(id+"F4.wireOp",EDGE,"E35.filletArc")])]})])],"derivedFrom":makeQuery(id+"F5.opExtrude","CAP_EDGE",EDGE,{"disambiguationData":[OSD([subQ0])],"isStart":false})});}
            var Q4;
            {var subQ0=sQuery(id+"F0.wireOp",EDGE,"E25.7");var subQ1=sQuery(id+"F0.wireOp",EDGE,"E25.1");var subQ2=sQuery(id+"F0.wireOp",EDGE,"E25.6");var subQ3=sQuery(id+"F0.wireOp",EDGE,"E25.5");var subQ4=sQuery(id+"F0.wireOp",EDGE,"E25.4");var subQ5=sQuery(id+"F0.wireOp",EDGE,"E25.0");var subQ6=sQuery(id+"F0.wireOp",EDGE,"E25.2");var subQ7=sQuery(id+"F0.wireOp",EDGE,"E25.3");Q4=makeQuery(id+"F8.boolean.opBoolean","INTERSECT",EDGE,{"derivedFrom":[makeQuery(id+"F5.boolean.opBoolean","SPLIT",FACE,{"disambiguationData":[TD([makeQuery(id+"F2.opExtrude","SWEPT_FACE",FACE,{"disambiguationData":[OSD([subQ5])]})])],"derivedFrom":makeQuery(id+"F3.boolean.opBoolean","COPY",FACE,{"derivedFrom":makeQuery(id+"F3.opExtrude","CAP_FACE",FACE,{"disambiguationData":[OSD([subQ5,subQ1,subQ6,subQ7,subQ4,subQ3,subQ2,subQ0])],"isStart":false})})}),makeQuery(id+"F8.opExtrude","SWEPT_FACE",FACE,{"disambiguationData":[OSD([sQuery(id+"F7.wireOp",EDGE,"E67")])]})]});}
            var Q5;
            Q5=makeQuery(id+"F8.boolean.opBoolean","INTERSECT",EDGE,{"disambiguationData":[OD(0.0)],"derivedFrom":[makeQuery(id+"F5.opExtrude","SWEPT_FACE",FACE,{"disambiguationData":[OSD([sQuery(id+"F4.wireOp",EDGE,"E30")])]}),makeQuery(id+"F8.opExtrude","SWEPT_FACE",FACE,{"disambiguationData":[OSD([sQuery(id+"F7.wireOp",EDGE,"E67")])]})]});
            fillet(context, id + "F14", {"entities" : qUnion([Q0, Q1, Q2, Q3, Q4, Q5]), "radius" : 3 * mm, "tangentPropagation" : true, "allowEdgeOverflow" : false});
        }
        {
            var Q0;
            Q0=makeQuery(id+"F1.opExtrude","CAP_EDGE",EDGE,{"disambiguationData":[OSD([sQuery(id+"F0.wireOp",EDGE,"E1.bottom")])],"isStart":false});
            fillet(context, id + "F15", {"entities" : qUnion([Q0]), "radius" : 2 * mm, "tangentPropagation" : true, "allowEdgeOverflow" : false});
        }
        {
            var Q0;
            {var subQ0=sQuery(id+"F0.wireOp",EDGE,"E21.filletArc");var subQ1=sQuery(id+"F0.wireOp",EDGE,"E7");var subQ2=sQuery(id+"F0.wireOp",EDGE,"E6");var subQ3=sQuery(id+"F0.wireOp",EDGE,"E5");var subQ4=sQuery(id+"F0.wireOp",EDGE,"E4");var subQ5=sQuery(id+"F0.wireOp",EDGE,"E22.filletArc");var subQ6=sQuery(id+"F0.wireOp",EDGE,"E1.bottom");var subQ7=sQuery(id+"F0.wireOp",EDGE,"E1.right");var subQ8=sQuery(id+"F0.wireOp",EDGE,"E1.top");var subQ9=sQuery(id+"F0.wireOp",EDGE,"E1.left");var subQ10=sQuery(id+"F0.wireOp",EDGE,"E23.filletArc");var subQ11=sQuery(id+"F0.wireOp",EDGE,"E24.filletArc");Q0=makeQuery(id+"F2.boolean.opBoolean","SPLIT",FACE,{"disambiguationData":[TD([makeQuery(id+"F1.opExtrude","SWEPT_FACE",FACE,{"disambiguationData":[OSD([subQ6])]})])],"derivedFrom":makeQuery(id+"F1.opExtrude","CAP_FACE",FACE,{"disambiguationData":[OSD([subQ6,subQ8,subQ9,subQ7,subQ4,subQ3,subQ2,subQ1,subQ0,subQ5,subQ10,subQ11])],"isStart":true})});}
            var sketch = newSketch(context, id + "F16", { "sketchPlane" : qUnion([Q0])});
            skLineSegment(sketch, "E79", {"start": v(0, 90) * mm, "end": v(0, 120) * mm, "construction": true});
            skCircle(sketch, "E80", {"center": v(0, 120) * mm, "radius": 6 * mm});
            skLineSegment(sketch, "E81", {"start": v(-33, 90) * mm, "end": v(-15, 108) * mm});
            skLineSegment(sketch, "E82", {"start": v(-15, 108) * mm, "end": v(-15, 120) * mm});
            skLineSegment(sketch, "E83", {"start": v(33, 90) * mm, "end": v(15, 108) * mm});
            skLineSegment(sketch, "E84", {"start": v(15, 108) * mm, "end": v(15, 120) * mm});
            skArc(sketch, "E85", {"start": v(15, 120) * mm, "mid": v(0, 135) * mm, "end": v(-15, 120) * mm});
            skLineSegment(sketch, "E86", {"start": v(-80, 0) * mm, "end": v(80, 0) * mm, "construction": true});
            skLineSegment(sketch, "E87.MirrorCS", {"start": v(33, -90) * mm, "end": v(15, -108) * mm});
            skLineSegment(sketch, "E88.MirrorCS", {"start": v(-15, -108) * mm, "end": v(-15, -120) * mm});
            skLineSegment(sketch, "E89.MirrorCS", {"start": v(-33, -90) * mm, "end": v(-15, -108) * mm});
            skLineSegment(sketch, "E90.MirrorCS", {"start": v(0, -90) * mm, "end": v(0, -120) * mm, "construction": true});
            skArc(sketch, "E91.MirrorCS", {"start": v(15, -120) * mm, "mid": v(0, -135) * mm, "end": v(-15, -120) * mm});
            skLineSegment(sketch, "E92.MirrorCS", {"start": v(15, -108) * mm, "end": v(15, -120) * mm});
            skCircle(sketch, "E93.MirrorC", {"center": v(0, -120) * mm, "radius": 6 * mm});
            skSolve(sketch);
        }
        {
            var Q0;
            Q0=makeQuery(id+"F16.imprint","IMPRINT",FACE,{"disambiguationData":[TD([[makeQuery(id+"F16.imprint","IMPRINT",EDGE,{"derivedFrom":sQuery(id+"F16.wireOp",EDGE,"E80")}),-1.0]])]});
            var Q1;
            Q1=makeQuery(id+"F16.imprint","IMPRINT",FACE,{"disambiguationData":[TD([[makeQuery(id+"F16.imprint","IMPRINT",EDGE,{"derivedFrom":makeQuery(id+"F1.opExtrude","CAP_EDGE",EDGE,{"disambiguationData":[OSD([sQuery(id+"F0.wireOp",EDGE,"E1.left")])],"isStart":true})}),-1.0]])]});
            var Q2;
            {var subQ1=sQuery(id+"F16.wireOp",EDGE,"E87.MirrorCS");Q2=makeQuery(id+"F16.imprint","IMPRINT",FACE,{"disambiguationData":[TD([[makeQuery(id+"F16.imprint","IMPRINT",EDGE,{"derivedFrom":subQ1}),-1.0]])]});}
            var Q3;
            Q3=makeQuery(id+"F2.opExtrude","CAP_FACE",FACE,{"disambiguationData":[OSD([sQuery(id+"F0.wireOp",EDGE,"E12"),sQuery(id+"F0.wireOp",EDGE,"E13"),sQuery(id+"F0.wireOp",EDGE,"E14"),sQuery(id+"F0.wireOp",EDGE,"E15"),sQuery(id+"F0.wireOp",EDGE,"E17.filletArc"),sQuery(id+"F0.wireOp",EDGE,"E18.filletArc"),sQuery(id+"F0.wireOp",EDGE,"E19.filletArc"),sQuery(id+"F0.wireOp",EDGE,"E20.filletArc"),sQuery(id+"F0.wireOp",EDGE,"E25.0"),sQuery(id+"F0.wireOp",EDGE,"E25.1"),sQuery(id+"F0.wireOp",EDGE,"E25.2"),sQuery(id+"F0.wireOp",EDGE,"E25.3"),sQuery(id+"F0.wireOp",EDGE,"E25.4"),sQuery(id+"F0.wireOp",EDGE,"E25.5"),sQuery(id+"F0.wireOp",EDGE,"E25.6"),sQuery(id+"F0.wireOp",EDGE,"E25.7")])],"isStart":false});
            extrude(context, id + "F17", {"entities" : qUnion([Q0, Q1, Q2]), "endBound" : BoundingType.UP_TO_SURFACE, "depth" : 25 * mm, "endBoundEntityFace" : qUnion([Q3]), "offsetDistance" : 25 * mm});
        }
    });
